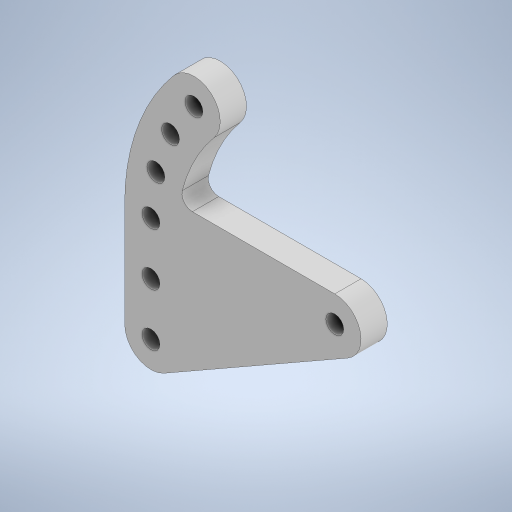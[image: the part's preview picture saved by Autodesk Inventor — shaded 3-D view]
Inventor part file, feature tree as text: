
AUTODESK INVENTOR PART (.ipt)
format: ipt  version: 2024.3 (Build 283343010, 343A)  size: 320,512 bytes
history: native  units: mm
features: sketch x7, extrude x5, projected_geometry x3, hole x2, other x1, fillet x1
ambient origin geometry x8: Origin, YZ Plane, XZ Plane, XY Plane, X Axis, Y Axis, Z Axis, Center Point
bodies: Body1 (feature_tree)
feature tree (19):
  other  "ソリッド1"
  extrude  "押し出し1"  Depth=80.0mm
  extrude  "押し出し2"  Depth=5.0mm TaperAngle=0.0deg
  hole  "穴1"  [1 undecoded]
  extrude  "押し出し3"  Depth=5.0mm
  extrude  "押し出し5"  Depth=10.0mm
  hole  "穴3"  [1 undecoded]
  extrude  "押し出し6"  Depth=70.0mm
  fillet  "フィレット1"  Radius=40.0mm
  sketch  "スケッチ1"
  sketch  "スケッチ2"
  projected_geometry  "投影ループ1"
  sketch  "スケッチ3"
  sketch  "スケッチ4"
  projected_geometry  "投影ループ2"
  sketch  "スケッチ7"
  sketch  "スケッチ8"
  sketch  "スケッチ9"
  projected_geometry  "投影ループ3"
note: 2 required parameter values undecoded (feature->parameter linkage not recoverable at this tier; creation-order binding heuristic only, values carry confidence <= 0.55)
